# Revit family: Kohler Singulier 10877A-4-CP Family
name_source: partatom
category: Plumbing Fixtures
revit_build: Autodesk Revit 2018 (Build: 20170223_1515(x64)
units: mm (PartAtom-declared; Revit-internal decimal feet)

## family parameters
Cut with Voids When Loaded = No
Host = Face
Part Type = Normal
Room Calculation Point = No
Round Connector Dimension = Use Diameter
Shared = No

## types (1)
- Kohler Singulier 10877A-4-CP Family
    Default Elevation = 1219 mm
    Description = SINGULIER KITCHEN MIXER
    Disclamer = Block C unit 2, Coachman's Crossing Office Park, 4 Brian St, Lyme Park, Johannesburg, 2191
    Manufacturer = Kohler CO
    Material = Faucets
    Model = 10877A-4-CP
    Telephone = 011 050 9000
    Total Height = 336 mm  [stored 1.10236 ft]
    Total Width = 239 mm  [stored 0.784121 ft]
    URL = http://www.africa.kohler.com

note: [stored X ft] marks values corroborated as IEEE doubles in the binary element streams (Revit-internal decimal feet)

## geometry (parser evidence)
native form markers: Sweep x2
no freeform markers — native parametric forms only
